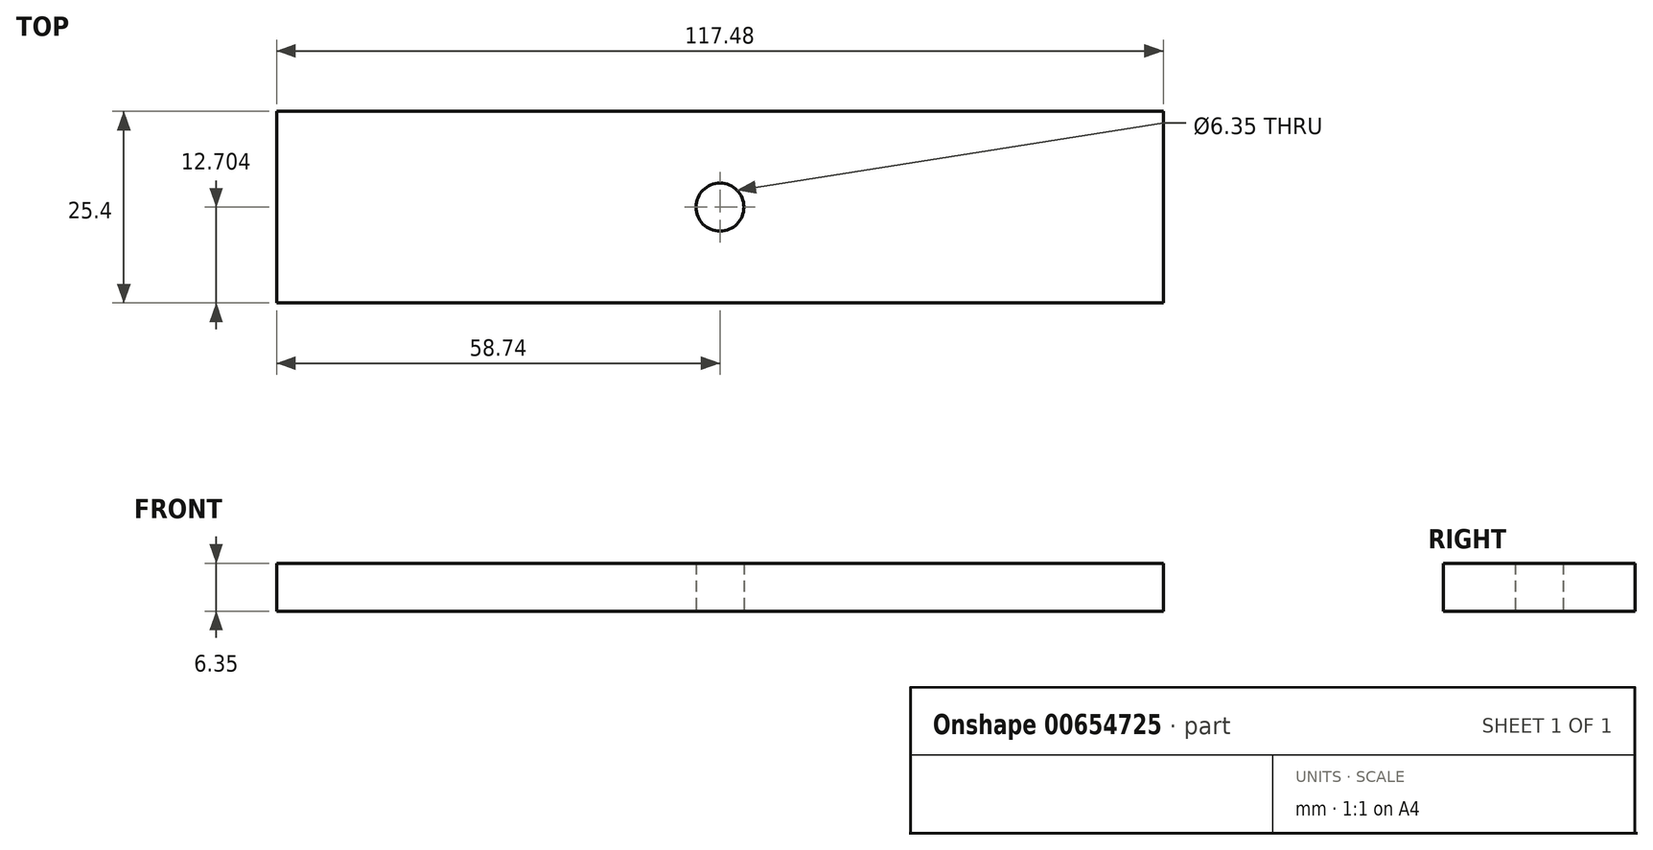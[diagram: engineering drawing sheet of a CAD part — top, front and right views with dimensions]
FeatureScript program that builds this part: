
annotation { "Feature Type Name" : "Feature", "Feature Type Description" : "" }
export const myFeature = defineFeature(function(context is Context, id is Id, definition is map)
    precondition{}
    {
        {
            var Q0;
            Q0=qCreatedBy(makeId("Top.planeOp"),FACE);
            var sketch = newSketch(context, id + "F0", { "sketchPlane" : qUnion([Q0])});
            skLineSegment(sketch, "E0.bottom", {"start": v(-97.52, -11.78) * mm, "end": v(19.96, -11.78) * mm});
            skLineSegment(sketch, "E0.top", {"start": v(-97.52, 13.62) * mm, "end": v(19.96, 13.62) * mm});
            skLineSegment(sketch, "E0.left", {"start": v(-97.52, -11.78) * mm, "end": v(-97.52, 13.62) * mm});
            skLineSegment(sketch, "E0.right", {"start": v(19.96, -11.78) * mm, "end": v(19.96, 13.62) * mm});
            skCircle(sketch, "E1", {"center": v(-38.78, 0.92) * mm, "radius": 3.18 * mm});
            skPoint(sketch, "E1.centerSnap0", {"position": v(-97.52, 0.92) * mm});
            skSolve(sketch);
        }
        {
            var Q0;
            Q0 = qSketchRegion(id + "F0", true);
            extrude(context, id + "F1", {"entities" : qUnion([Q0]), "depth" : 6.35 * mm, "offsetDistance" : 25.4 * mm});
        }
    });
